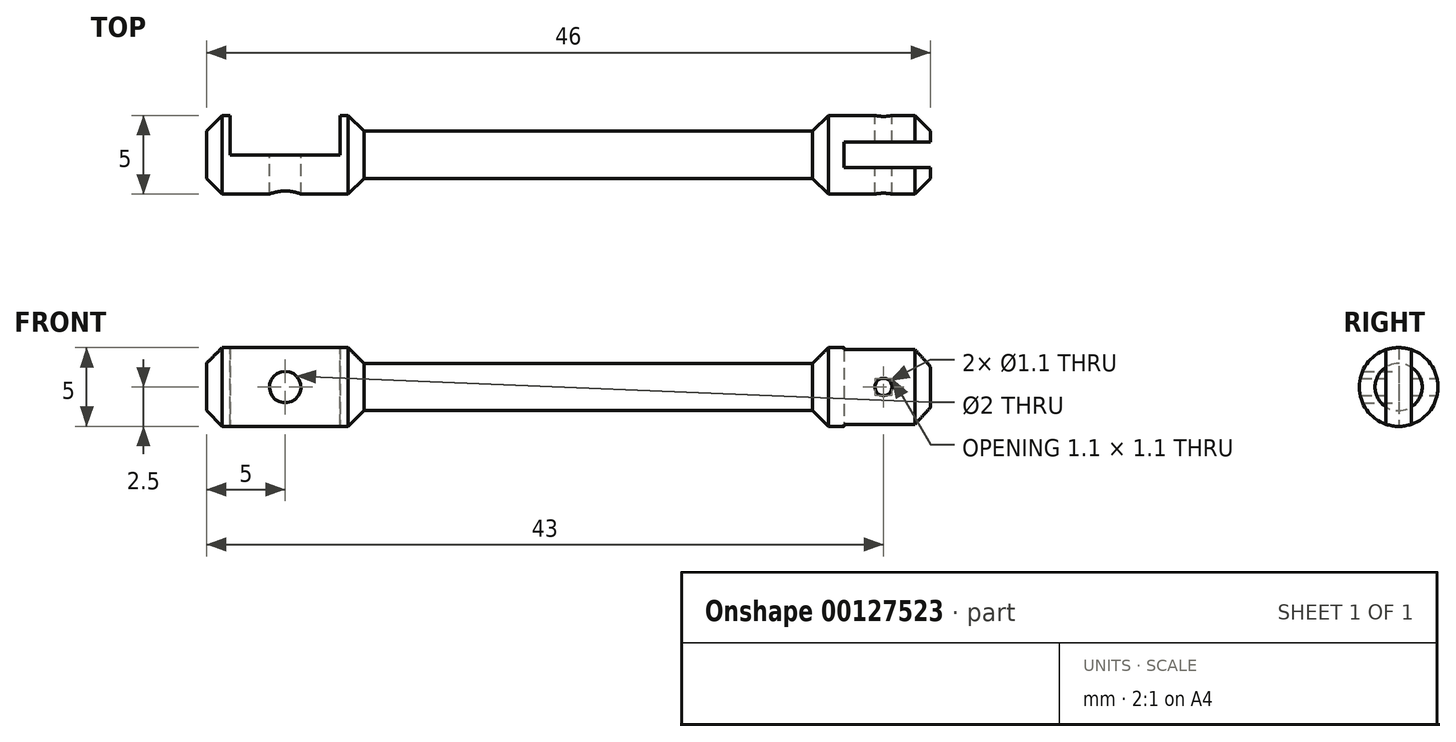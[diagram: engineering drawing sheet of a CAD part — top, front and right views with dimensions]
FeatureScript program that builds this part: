
annotation { "Feature Type Name" : "Feature", "Feature Type Description" : "" }
export const myFeature = defineFeature(function(context is Context, id is Id, definition is map)
    precondition{}
    {
        {
            var Q0;
            Q0=qCreatedBy(makeId("Front.planeOp"),FACE);
            var sketch = newSketch(context, id + "F0", { "sketchPlane" : qUnion([Q0])});
            skCircle(sketch, "E0", {"center": v(0, 0) * mm, "radius": 1 * mm});
            skCircle(sketch, "E1", {"center": v(38, 0) * mm, "radius": 0.55 * mm});
            skLineSegment(sketch, "E2", {"start": v(-5, 0) * mm, "end": v(41, 0) * mm});
            skLineSegment(sketch, "E3", {"start": v(41, 0) * mm, "end": v(41, 1.5) * mm});
            skLineSegment(sketch, "E4", {"start": v(40, 2.5) * mm, "end": v(34.5, 2.5) * mm});
            skLineSegment(sketch, "E5", {"start": v(33.5, 1.5) * mm, "end": v(5, 1.5) * mm});
            skLineSegment(sketch, "E6", {"start": v(4, 2.5) * mm, "end": v(-4, 2.5) * mm});
            skLineSegment(sketch, "E7", {"start": v(-5, 1.5) * mm, "end": v(-5, 0) * mm});
            skLineSegment(sketch, "E8", {"start": v(40, 2.5) * mm, "end": v(41, 1.5) * mm});
            skLineSegment(sketch, "E9", {"start": v(33.5, 1.5) * mm, "end": v(34.5, 2.5) * mm});
            skLineSegment(sketch, "E10", {"start": v(0, 0) * mm, "end": v(0, 0) * mm});
            skLineSegment(sketch, "E11", {"start": v(4, 2.5) * mm, "end": v(5, 1.5) * mm});
            skLineSegment(sketch, "E12", {"start": v(-4, 2.5) * mm, "end": v(-5, 1.5) * mm});
            skSolve(sketch);
        }
        {
            var Q0;
            {var subQ0=sQuery(id+"F0.wireOp",EDGE,"E3");Q0=makeQuery(id+"F0.imprint","IMPRINT",FACE,{"disambiguationData":[TD([[makeQuery(id+"F0.imprint","IMPRINT",EDGE,{"derivedFrom":subQ0}),1.0]])]});}
            var Q1;
            {var subQ0=sQuery(id+"F0.wireOp",EDGE,"E2");var subQ1=sQuery(id+"F0.wireOp",EDGE,"E0");var subQ2=makeQuery(id+"F0.imprint","INTERSECT",VERTEX,{"disambiguationData":[OD(0.0)],"derivedFrom":[subQ1,subQ0]});Q1=makeQuery(id+"F0.imprint","IMPRINT",FACE,{"disambiguationData":[TD([[makeQuery(id+"F0.imprint","IMPRINT",EDGE,{"disambiguationData":[TD([[subQ2,1.0]])],"derivedFrom":subQ1}),1.0]])]});}
            var Q2;
            {var subQ0=sQuery(id+"F0.wireOp",EDGE,"E2");var subQ1=sQuery(id+"F0.wireOp",EDGE,"E1");var subQ2=makeQuery(id+"F0.imprint","INTERSECT",VERTEX,{"disambiguationData":[OD(0.0)],"derivedFrom":[subQ1,subQ0]});Q2=makeQuery(id+"F0.imprint","IMPRINT",FACE,{"disambiguationData":[TD([[makeQuery(id+"F0.imprint","IMPRINT",EDGE,{"disambiguationData":[TD([[subQ2,1.0]])],"derivedFrom":subQ1}),1.0]])]});}
            var Q3;
            Q3=sQuery(id+"F0.wireOp",EDGE,"E2");
            revolve(context, id + "F1", {"entities" : qUnion([Q0, Q1, Q2]), "axis" : qUnion([Q3]), "revolveType" : RevolveType.FULL});
        }
        {
            var Q0;
            {var subQ0=sQuery(id+"F0.wireOp",EDGE,"E2");var subQ1=sQuery(id+"F0.wireOp",EDGE,"E0");var subQ2=makeQuery(id+"F0.imprint","INTERSECT",VERTEX,{"disambiguationData":[OD(0.0)],"derivedFrom":[subQ1,subQ0]});Q0=makeQuery(id+"F0.imprint","IMPRINT",FACE,{"disambiguationData":[TD([[makeQuery(id+"F0.imprint","IMPRINT",EDGE,{"disambiguationData":[TD([[subQ2,-1.0]])],"derivedFrom":subQ1}),1.0]])]});}
            var Q1;
            {var subQ0=sQuery(id+"F0.wireOp",EDGE,"E2");var subQ1=sQuery(id+"F0.wireOp",EDGE,"E0");var subQ2=makeQuery(id+"F0.imprint","INTERSECT",VERTEX,{"disambiguationData":[OD(0.0)],"derivedFrom":[subQ1,subQ0]});Q1=makeQuery(id+"F0.imprint","IMPRINT",FACE,{"disambiguationData":[TD([[makeQuery(id+"F0.imprint","IMPRINT",EDGE,{"disambiguationData":[TD([[subQ2,1.0]])],"derivedFrom":subQ1}),1.0]])]});}
            var Q2;
            {var subQ0=sQuery(id+"F0.wireOp",EDGE,"E2");var subQ1=sQuery(id+"F0.wireOp",EDGE,"E1");var subQ2=makeQuery(id+"F0.imprint","INTERSECT",VERTEX,{"disambiguationData":[OD(0.0)],"derivedFrom":[subQ1,subQ0]});Q2=makeQuery(id+"F0.imprint","IMPRINT",FACE,{"disambiguationData":[TD([[makeQuery(id+"F0.imprint","IMPRINT",EDGE,{"disambiguationData":[TD([[subQ2,-1.0]])],"derivedFrom":subQ1}),1.0]])]});}
            var Q3;
            {var subQ0=sQuery(id+"F0.wireOp",EDGE,"E2");var subQ1=sQuery(id+"F0.wireOp",EDGE,"E1");var subQ2=makeQuery(id+"F0.imprint","INTERSECT",VERTEX,{"disambiguationData":[OD(0.0)],"derivedFrom":[subQ1,subQ0]});Q3=makeQuery(id+"F0.imprint","IMPRINT",FACE,{"disambiguationData":[TD([[makeQuery(id+"F0.imprint","IMPRINT",EDGE,{"disambiguationData":[TD([[subQ2,1.0]])],"derivedFrom":subQ1}),1.0]])]});}
            extrude(context, id + "F2", {"entities" : qUnion([Q0, Q1, Q2, Q3]), "operationType" : NewBodyOperationType.REMOVE, "endBound" : BoundingType.SYMMETRIC, "depth" : 25.4 * mm});
        }
        {
            var Q0;
            Q0=qCreatedBy(makeId("Top.planeOp"),FACE);
            var sketch = newSketch(context, id + "F3", { "sketchPlane" : qUnion([Q0])});
            skLineSegment(sketch, "E13.bottom", {"start": v(-3.5, 4.5) * mm, "end": v(3.5, 4.5) * mm});
            skLineSegment(sketch, "E13.top", {"start": v(-3.5, 0) * mm, "end": v(3.5, 0) * mm});
            skLineSegment(sketch, "E13.left", {"start": v(-3.5, 4.5) * mm, "end": v(-3.5, 0) * mm});
            skLineSegment(sketch, "E13.right", {"start": v(3.5, 4.5) * mm, "end": v(3.5, 0) * mm});
            skLineSegment(sketch, "E14.bottom", {"start": v(41, 0.8) * mm, "end": v(35.5, 0.8) * mm});
            skLineSegment(sketch, "E14.top", {"start": v(41, -0.8) * mm, "end": v(35.5, -0.8) * mm});
            skLineSegment(sketch, "E14.left", {"start": v(41, 0.8) * mm, "end": v(41, -0.8) * mm});
            skLineSegment(sketch, "E14.right", {"start": v(35.5, 0.8) * mm, "end": v(35.5, -0.8) * mm});
            skLineSegment(sketch, "E15", {"start": v(-7.5, 0) * mm, "end": v(53.61, 0) * mm, "construction": true});
            skLineSegment(sketch, "E16", {"start": v(0, 0) * mm, "end": v(0, 7.28) * mm, "construction": true});
            skSolve(sketch);
        }
        {
            var Q0;
            Q0 = qSketchRegion(id + "F3", true);
            extrude(context, id + "F4", {"entities" : qUnion([Q0]), "operationType" : NewBodyOperationType.REMOVE, "endBound" : BoundingType.SYMMETRIC, "depth" : 25.4 * mm});
        }
    });
